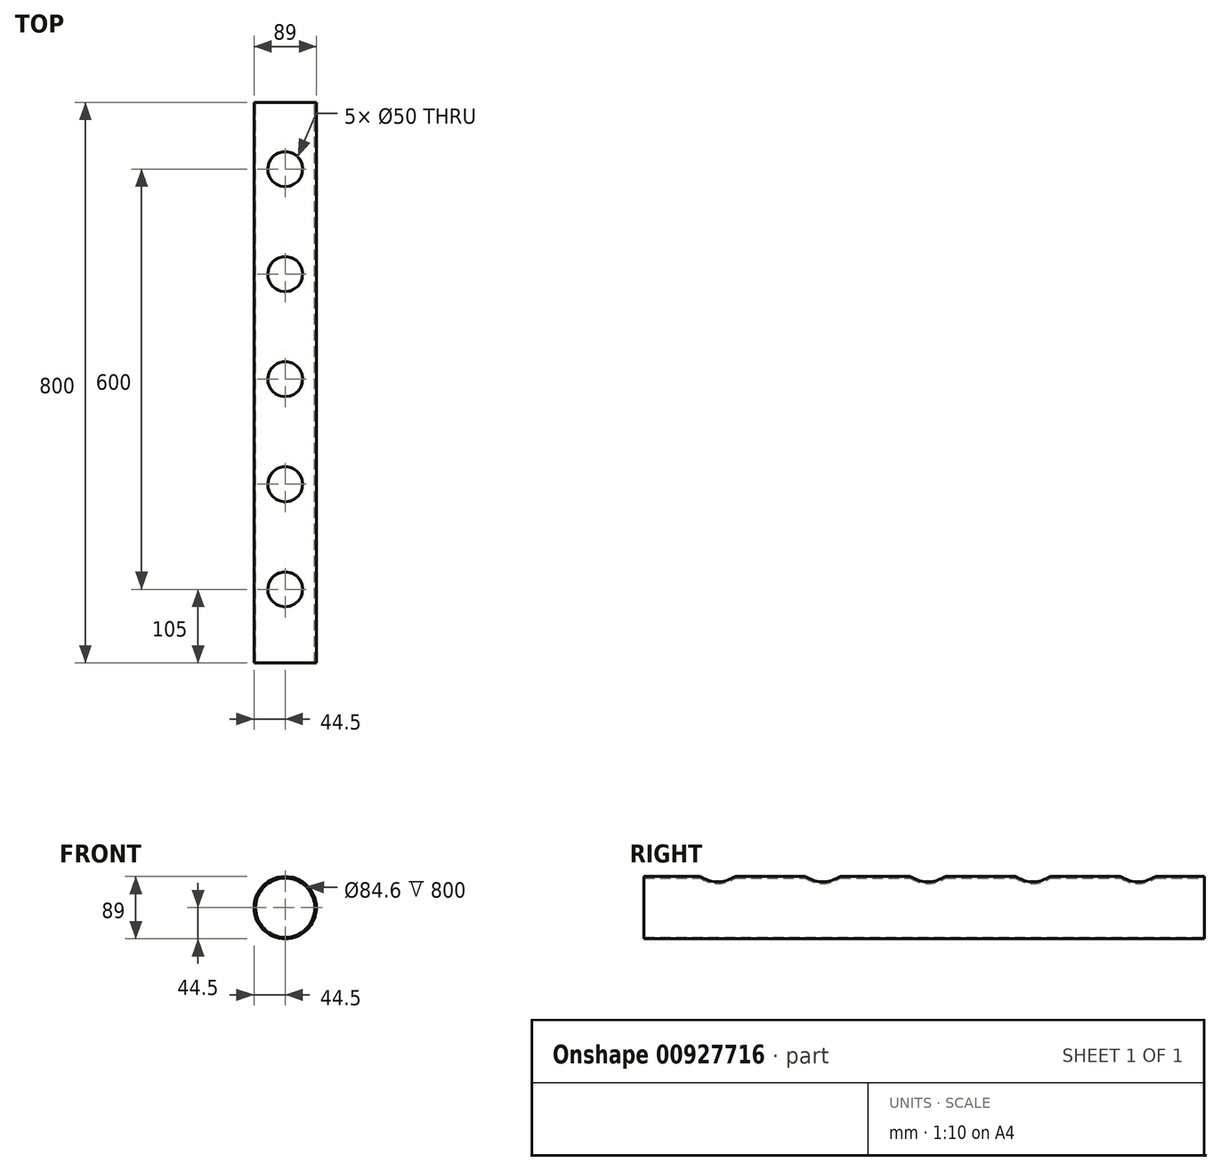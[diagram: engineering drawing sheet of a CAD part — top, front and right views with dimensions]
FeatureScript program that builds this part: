
annotation { "Feature Type Name" : "Feature", "Feature Type Description" : "" }
export const myFeature = defineFeature(function(context is Context, id is Id, definition is map)
    precondition{}
    {
        {
            var Q0;
            Q0=qCreatedBy(makeId("Front.planeOp"),FACE);
            var sketch = newSketch(context, id + "F0", { "sketchPlane" : qUnion([Q0])});
            skCircle(sketch, "E0", {"center": v(0, 0) * mm, "radius": 44.5 * mm});
            skCircle(sketch, "E1.0", {"center": v(0, 0) * mm, "radius": 42.3 * mm});
            skSolve(sketch);
        }
        {
            var Q0;
            Q0=makeQuery(id+"F0.imprint","IMPRINT",FACE,{"disambiguationData":[TD([[makeQuery(id+"F0.imprint","IMPRINT",EDGE,{"derivedFrom":sQuery(id+"F0.wireOp",EDGE,"E0")}),1.0]])]});
            extrude(context, id + "F1", {"entities" : qUnion([Q0]), "depth" : 800 * mm, "offsetDistance" : 25 * mm});
        }
        {
            var Q0;
            Q0=qCreatedBy(makeId("Top.planeOp"),FACE);
            var sketch = newSketch(context, id + "F2", { "sketchPlane" : qUnion([Q0])});
            skCircle(sketch, "E2", {"center": v(0, -95) * mm, "radius": 25 * mm});
            skCircle(sketch, "E3.0.1.0", {"center": v(0, -245) * mm, "radius": 25 * mm});
            skCircle(sketch, "E3.0.2.0", {"center": v(0, -395) * mm, "radius": 25 * mm});
            skCircle(sketch, "E3.0.3.0", {"center": v(0, -545) * mm, "radius": 25 * mm});
            skCircle(sketch, "E3.0.4.0", {"center": v(0, -695) * mm, "radius": 25 * mm});
            skLineSegment(sketch, "E3.direction1", {"start": v(0, -95) * mm, "end": v(25, -95) * mm, "construction": true});
            skLineSegment(sketch, "E3.direction2", {"start": v(0, -95) * mm, "end": v(0, -245) * mm, "construction": true});
            skSolve(sketch);
        }
        {
            var Q0;
            Q0 = qSketchRegion(id + "F2", true);
            extrude(context, id + "F3", {"entities" : qUnion([Q0]), "operationType" : NewBodyOperationType.REMOVE, "endBound" : BoundingType.THROUGH_ALL, "depth" : 25 * mm, "offsetDistance" : 25 * mm});
        }
    });
